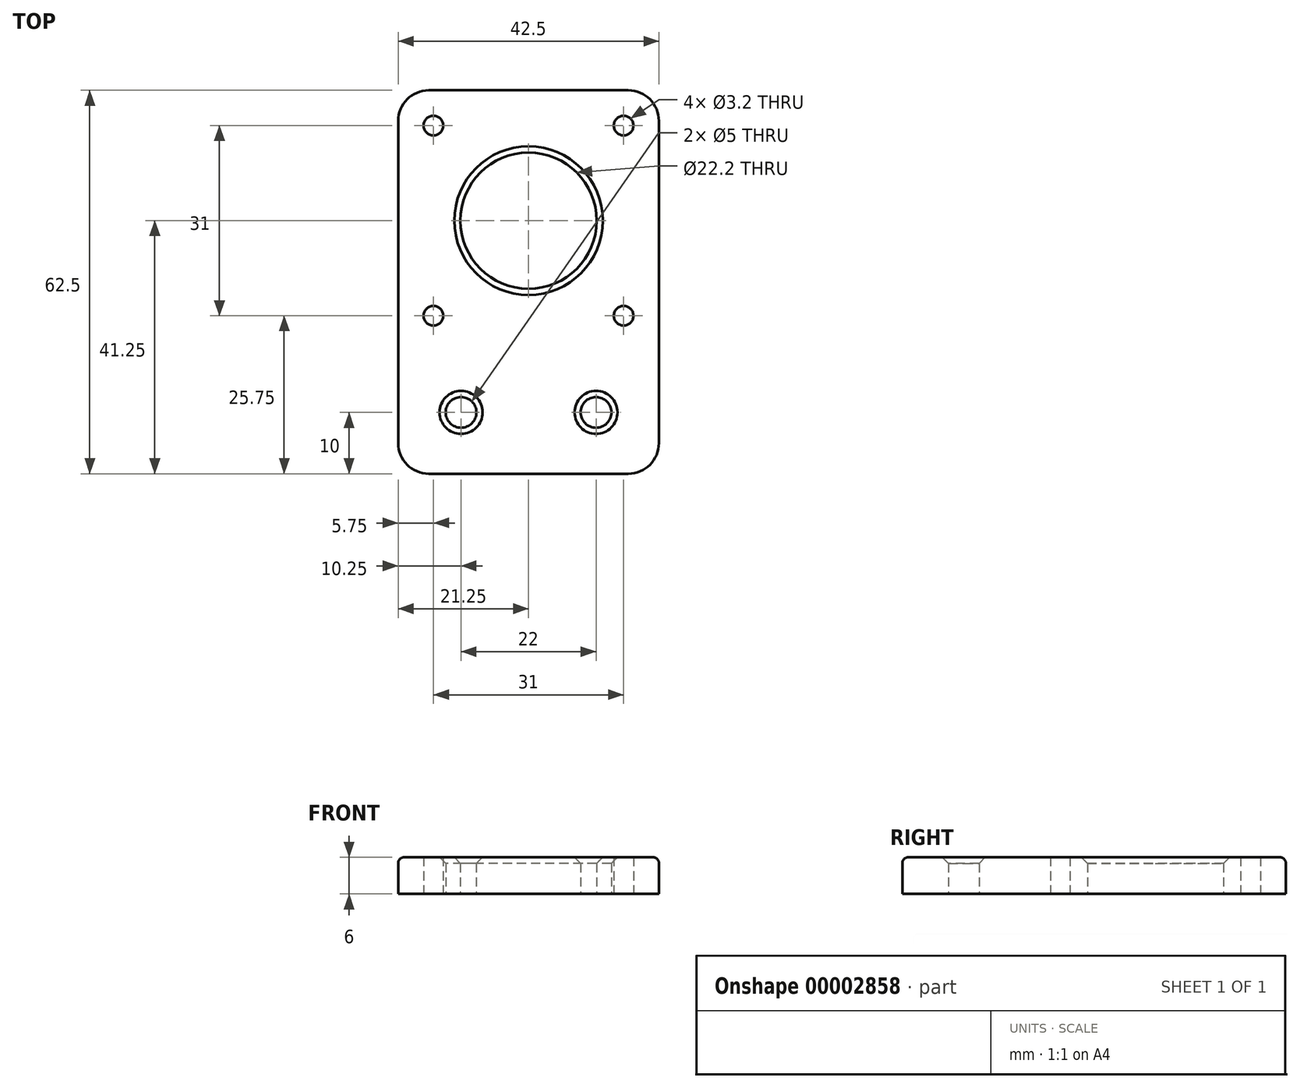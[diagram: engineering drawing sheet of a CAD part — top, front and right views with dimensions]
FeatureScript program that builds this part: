
annotation { "Feature Type Name" : "Feature", "Feature Type Description" : "" }
export const myFeature = defineFeature(function(context is Context, id is Id, definition is map)
    precondition{}
    {
        {
            var Q0;
            Q0=qCreatedBy(makeId("Top.planeOp"),FACE);
            var sketch = newSketch(context, id + "F0", { "sketchPlane" : qUnion([Q0])});
            skLineSegment(sketch, "E0.rect.bottom", {"start": v(15.5, 15.5) * mm, "end": v(-15.5, 15.5) * mm});
            skLineSegment(sketch, "E0.rect.top", {"start": v(15.5, -15.5) * mm, "end": v(-15.5, -15.5) * mm});
            skLineSegment(sketch, "E0.rect.left", {"start": v(15.5, 15.5) * mm, "end": v(15.5, -15.5) * mm});
            skLineSegment(sketch, "E0.rect.right", {"start": v(-15.5, 15.5) * mm, "end": v(-15.5, -15.5) * mm});
            skPoint(sketch, "E0.rect.middle", {"position": v(0, 0) * mm});
            skCircle(sketch, "E1", {"center": v(0, 0) * mm, "radius": 11.1 * mm});
            skCircle(sketch, "E2", {"center": v(-15.5, 15.5) * mm, "radius": 1.6 * mm});
            skCircle(sketch, "E3", {"center": v(15.5, 15.5) * mm, "radius": 1.6 * mm});
            skCircle(sketch, "E4", {"center": v(-15.5, -15.5) * mm, "radius": 1.6 * mm});
            skCircle(sketch, "E5", {"center": v(15.5, -15.5) * mm, "radius": 1.6 * mm});
            skLineSegment(sketch, "E6.rect.bottom", {"start": v(-16.25, 21.25) * mm, "end": v(16.25, 21.25) * mm});
            skLineSegment(sketch, "E6.rect.top", {"start": v(-21.25, -21.25) * mm, "end": v(21.25, -21.25) * mm});
            skLineSegment(sketch, "E6.rect.left", {"start": v(-21.25, 16.25) * mm, "end": v(-21.25, -21.25) * mm});
            skLineSegment(sketch, "E6.rect.right", {"start": v(21.25, 16.25) * mm, "end": v(21.25, -21.25) * mm});
            skLineSegment(sketch, "E7.top", {"start": v(-16.25, -41.25) * mm, "end": v(16.25, -41.25) * mm});
            skLineSegment(sketch, "E7.left", {"start": v(-21.25, -21.25) * mm, "end": v(-21.25, -36.25) * mm});
            skLineSegment(sketch, "E7.right", {"start": v(21.25, -21.25) * mm, "end": v(21.25, -36.25) * mm});
            skLineSegment(sketch, "E8", {"start": v(-21.25, -31.25) * mm, "end": v(21.25, -31.25) * mm});
            skCircle(sketch, "E9", {"center": v(-11, -31.25) * mm, "radius": 2.5 * mm});
            skCircle(sketch, "E10", {"center": v(11, -31.25) * mm, "radius": 2.5 * mm});
            skPoint(sketch, "E11.visualSharp", {"position": v(-21.25, 21.25) * mm});
            skArc(sketch, "E11.filletArc", {"start": v(-16.25, 21.25) * mm, "mid": v(-19.79, 19.79) * mm, "end": v(-21.25, 16.25) * mm});
            skPoint(sketch, "E12.visualSharp", {"position": v(21.25, 21.25) * mm});
            skArc(sketch, "E12.filletArc", {"start": v(21.25, 16.25) * mm, "mid": v(19.79, 19.79) * mm, "end": v(16.25, 21.25) * mm});
            skPoint(sketch, "E13.visualSharp", {"position": v(-21.25, -41.25) * mm});
            skArc(sketch, "E13.filletArc", {"start": v(-21.25, -36.25) * mm, "mid": v(-19.79, -39.79) * mm, "end": v(-16.25, -41.25) * mm});
            skPoint(sketch, "E14.visualSharp", {"position": v(21.25, -41.25) * mm});
            skArc(sketch, "E14.filletArc", {"start": v(16.25, -41.25) * mm, "mid": v(19.79, -39.79) * mm, "end": v(21.25, -36.25) * mm});
            skSolve(sketch);
        }
        {
            var Q0;
            Q0=makeQuery(id+"F0.imprint","IMPRINT",FACE,{"disambiguationData":[TD([[makeQuery(id+"F0.imprint","IMPRINT",EDGE,{"derivedFrom":sQuery(id+"F0.wireOp",EDGE,"E6.rect.bottom")}),-1.0]])]});
            var Q1;
            Q1=makeQuery(id+"F0.imprint","IMPRINT",FACE,{"disambiguationData":[TD([[makeQuery(id+"F0.imprint","IMPRINT",EDGE,{"derivedFrom":sQuery(id+"F0.wireOp",EDGE,"E1")}),-1.0]])]});
            var Q2;
            {var subQ11=sQuery(id+"F0.wireOp",EDGE,"E6.rect.top");Q2=makeQuery(id+"F0.imprint","IMPRINT",FACE,{"disambiguationData":[TD([[makeQuery(id+"F0.imprint","IMPRINT",EDGE,{"derivedFrom":subQ11}),-1.0]])]});}
            var Q3;
            Q3=makeQuery(id+"F0.imprint","IMPRINT",FACE,{"disambiguationData":[TD([[makeQuery(id+"F0.imprint","IMPRINT",EDGE,{"derivedFrom":sQuery(id+"F0.wireOp",EDGE,"E7.top")}),1.0]])]});
            extrude(context, id + "F1", {"entities" : qUnion([Q0, Q1, Q2, Q3]), "depth" : 6 * mm});
        }
        {
            var Q0;
            Q0=makeQuery(id+"F1.opExtrude","CAP_EDGE",EDGE,{"disambiguationData":[OSD([sQuery(id+"F0.wireOp",EDGE,"E1")])],"isStart":false});
            var Q1;
            Q1=makeQuery(id+"F1.opExtrude","CAP_EDGE",EDGE,{"disambiguationData":[OSD([sQuery(id+"F0.wireOp",EDGE,"E9")])],"isStart":false});
            var Q2;
            Q2=makeQuery(id+"F1.opExtrude","CAP_EDGE",EDGE,{"disambiguationData":[OSD([sQuery(id+"F0.wireOp",EDGE,"E10")])],"isStart":false});
            chamfer(context, id + "F2", {"entities" : qUnion([Q0, Q1, Q2]), "width" : 1 * mm, "tangentPropagation" : true});
        }
        {
            var Q0;
            Q0=makeQuery(id+"F1.opExtrude","CAP_EDGE",EDGE,{"disambiguationData":[OSD([sQuery(id+"F0.wireOp",EDGE,"E6.rect.bottom")])],"isStart":false});
            fillet(context, id + "F3", {"entities" : qUnion([Q0]), "radius" : 1 * mm, "tangentPropagation" : true, "allowEdgeOverflow" : false});
        }
    });
